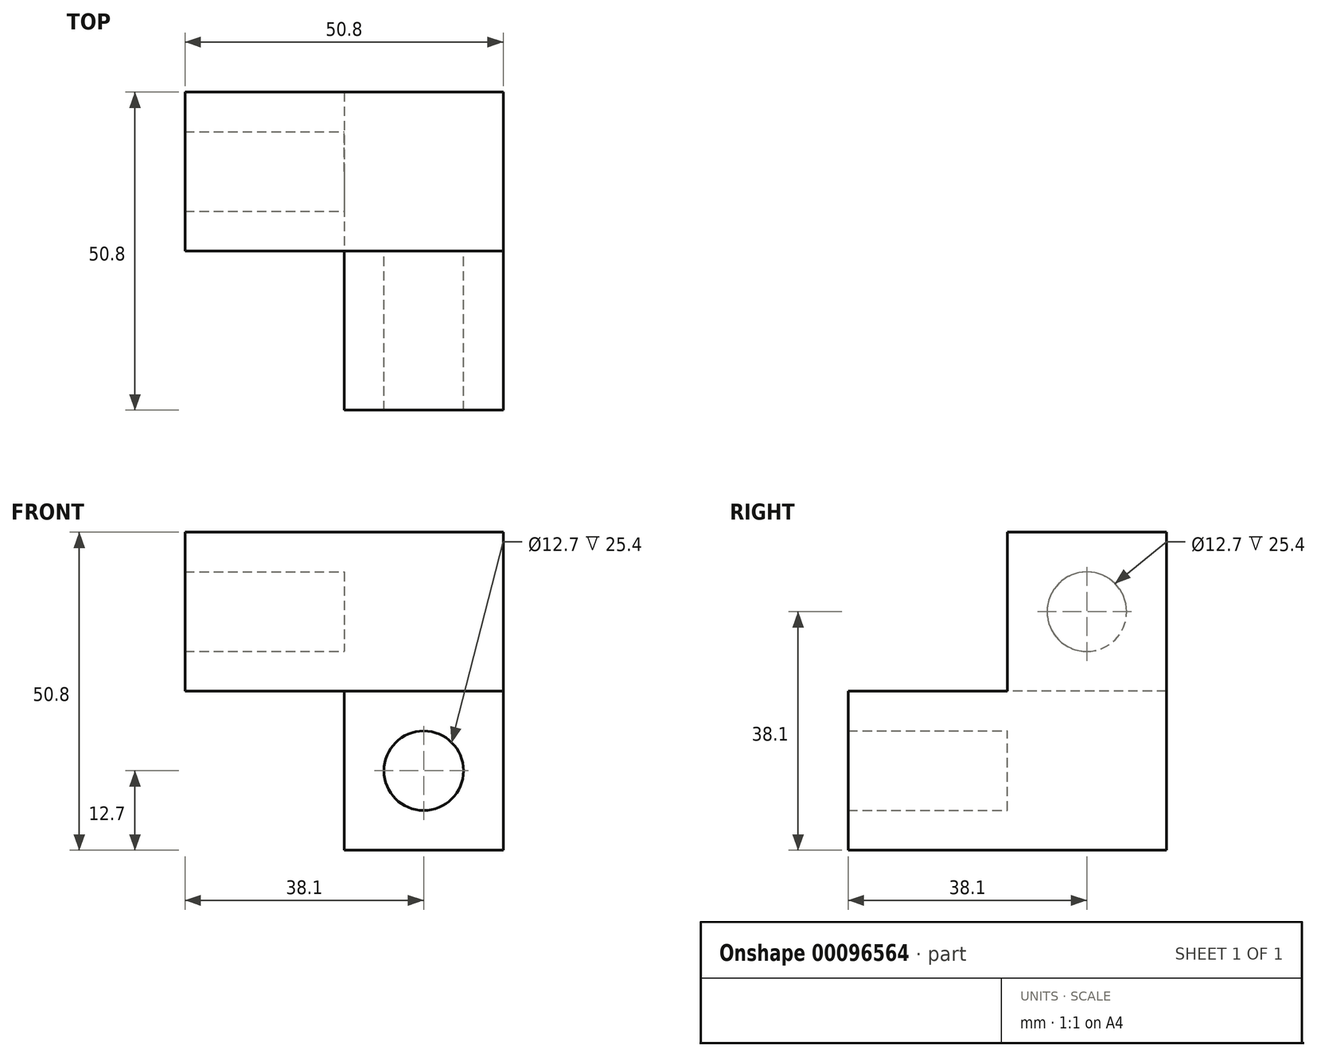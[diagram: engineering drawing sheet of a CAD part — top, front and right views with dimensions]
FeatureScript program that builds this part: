
annotation { "Feature Type Name" : "Feature", "Feature Type Description" : "" }
export const myFeature = defineFeature(function(context is Context, id is Id, definition is map)
    precondition{}
    {
        {
            var Q0;
            Q0=qCreatedBy(makeId("Front.planeOp"),FACE);
            var sketch = newSketch(context, id + "F0", { "sketchPlane" : qUnion([Q0])});
            skLineSegment(sketch, "E0.bottom", {"start": v(12.7, -25.4) * mm, "end": v(-12.7, -25.4) * mm});
            skLineSegment(sketch, "E0.top", {"start": v(12.7, 25.4) * mm, "end": v(-12.7, 25.4) * mm});
            skLineSegment(sketch, "E0.left", {"start": v(12.7, -25.4) * mm, "end": v(12.7, 25.4) * mm});
            skLineSegment(sketch, "E0.right", {"start": v(-12.7, -25.4) * mm, "end": v(-12.7, 25.4) * mm});
            skPoint(sketch, "E0.middle", {"position": v(0, 0) * mm});
            skSolve(sketch);
        }
        {
            var Q0;
            Q0=qSketchRegion(id+"F0",true);
            extrude(context, id + "F1", {"entities" : qUnion([Q0]), "depth" : 25.4 * mm, "symmetric" : true});
        }
        {
            var Q0;
            Q0=makeQuery(id+"F1.opExtrude","CAP_FACE",FACE,{"disambiguationData":[OSD([sQuery(id+"F0.wireOp",EDGE,"E0.bottom"),sQuery(id+"F0.wireOp",EDGE,"E0.top"),sQuery(id+"F0.wireOp",EDGE,"E0.left"),sQuery(id+"F0.wireOp",EDGE,"E0.right")])],"isStart":false});
            var sketch = newSketch(context, id + "F2", { "sketchPlane" : qUnion([Q0])});
            skLineSegment(sketch, "E1", {"start": v(0, -25.4) * mm, "end": v(0, 0) * mm, "construction": true});
            skLineSegment(sketch, "E2.bottom", {"start": v(-12.7, 0) * mm, "end": v(12.7, 0) * mm});
            skLineSegment(sketch, "E2.top", {"start": v(-12.7, -25.4) * mm, "end": v(12.7, -25.4) * mm});
            skLineSegment(sketch, "E2.left", {"start": v(-12.7, 0) * mm, "end": v(-12.7, -25.4) * mm});
            skLineSegment(sketch, "E2.right", {"start": v(12.7, 0) * mm, "end": v(12.7, -25.4) * mm});
            skLineSegment(sketch, "E3", {"start": v(-12.7, -12.7) * mm, "end": v(12.7, -12.7) * mm, "construction": true});
            skCircle(sketch, "E4", {"center": v(0, -12.7) * mm, "radius": 6.35 * mm});
            skSolve(sketch);
        }
        {
            var Q0;
            Q0=makeQuery(id+"F1.opExtrude","SWEPT_FACE",FACE,{"disambiguationData":[OSD([sQuery(id+"F0.wireOp",EDGE,"E0.left")])]});
            var sketch = newSketch(context, id + "F3", { "sketchPlane" : qUnion([Q0])});
            skLineSegment(sketch, "E5.bottom", {"start": v(-12.7, 25.4) * mm, "end": v(12.7, 25.4) * mm});
            skLineSegment(sketch, "E5.top", {"start": v(-12.7, 0) * mm, "end": v(12.7, 0) * mm});
            skLineSegment(sketch, "E5.left", {"start": v(-12.7, 25.4) * mm, "end": v(-12.7, 0) * mm});
            skLineSegment(sketch, "E5.right", {"start": v(12.7, 25.4) * mm, "end": v(12.7, 0) * mm});
            skLineSegment(sketch, "E6", {"start": v(0, 0) * mm, "end": v(0, 25.4) * mm, "construction": true});
            skLineSegment(sketch, "E7", {"start": v(-12.7, 12.7) * mm, "end": v(12.7, 12.7) * mm, "construction": true});
            skCircle(sketch, "E8", {"center": v(0, 12.7) * mm, "radius": 6.35 * mm});
            skSolve(sketch);
        }
        {
            var Q0;
            Q0=qSketchRegion(id+"F3",true);
            extrude(context, id + "F4", {"entities" : qUnion([Q0]), "operationType" : NewBodyOperationType.ADD, "oppositeDirection" : true, "depth" : 50.8 * mm});
        }
        {
            var Q0;
            Q0=qSketchRegion(id+"F2",true);
            extrude(context, id + "F5", {"entities" : qUnion([Q0]), "operationType" : NewBodyOperationType.ADD, "depth" : 25.4 * mm});
        }
    });
